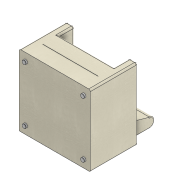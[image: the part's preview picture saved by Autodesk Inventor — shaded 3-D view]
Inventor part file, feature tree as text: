
AUTODESK INVENTOR PART (.ipt)
format: ipt  version: 2020.2 (Build 242310000, 310)  size: 352,768 bytes
history: native  units: mm
features: fillet x7, extrude x6, sketch x6, plane x4
ambient origin geometry x8: Origin, YZ Plane, XZ Plane, XY Plane, X Axis, Y Axis, Z Axis, Center Point
bodies: Solid1 (feature_tree), Solid2 (feature_tree)
feature tree (23):
  extrude  "Extrusion1"  Depth=900.0mm
  plane  "Work Plane1"
  sketch  "Sketch4"  dims[d4=0.0mm d5=2.0mm]
  fillet  "Fillet1"  Radius=200.0mm
  extrude  "Extrusion2"  Depth=2.0mm
  plane  "Work Plane2"
  extrude  "Extrusion3"  TaperAngle=0.0deg  [1 undecoded]
  fillet  "Fillet2"  Radius=600.0mm
  fillet  "Fillet3"  Radius=100.0mm
  plane  "Work Plane3"
  extrude  "Extrusion4"  Depth=20.0mm
  sketch  "Sketch7"  dims[d16=900.0mm d17=100.0mm d18=0.0mm d21=450.0mm]
  fillet  "Fillet6"  [1 undecoded]
  fillet  "Fillet7"  Radius=600.0mm
  extrude  "Extrusion5"  Depth=100.0mm TaperAngle=0.0deg
  fillet  "Fillet8"  Radius=450.0mm
  plane  "Work Plane4"
  extrude  "Extrusion6"  Depth=10.0mm
  fillet  "Fillet9"  Radius=700.0mm
  sketch  "Sketch3"  dims[d0=700.0mm d1=900.0mm d2=200.0mm d3=0.0mm]
  sketch  "Sketch5"  dims[d6=200.0mm d7=0.0mm d8=0.0mm d9=600.0mm d10=100.0mm d11=0.0mm]
  sketch  "Sketch6"  dims[d12=20.0mm d13=20.0mm d14=0.0mm d15=600.0mm]
  sketch  "Sketch8"  dims[d23=20.0mm d24=10.0mm d25=700.0mm d26=0.0mm d27=10.0mm d28=10.0mm d29=0.0mm d32=50.0mm d36=50.0mm d37=20.0mm d38=0.0mm d39=2.0mm]
note: 2 required parameter values undecoded (feature->parameter linkage not recoverable at this tier; creation-order binding heuristic only, values carry confidence <= 0.55)
